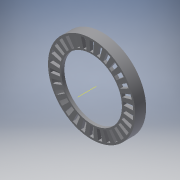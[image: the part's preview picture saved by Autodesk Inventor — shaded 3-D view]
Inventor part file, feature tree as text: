
AUTODESK INVENTOR PART (.ipt)
format: ipt  version: 2016 (Build 200138000, 138)  size: 313,344 bytes
history: native  units: mm
features: extrude x3, sketch x3, other x1, pattern_circular x1
ambient origin geometry x8: Origin, YZ Plane, XZ Plane, XY Plane, X Axis, Y Axis, Z Axis, Center Point
bodies: Body1 (feature_tree)
feature tree (8):
  extrude  "Extrusion3"  Depth=53.5mm
  extrude  "Extrusion4"  Depth=39.0mm
  other  "Work Axis3"
  pattern_circular  "Circular Pattern2"  [2 undecoded]
  extrude  "Extrusion5"  Depth=5.0mm
  sketch  "Sketch1"  dims[d0=56.0mm d1=53.5mm]
  sketch  "Sketch4"  dims[d2=41.0mm d3=39.0mm]
  sketch  "Sketch5"  dims[d13=8.5mm d17=3.0mm d18=3.0mm d19=4.0mm d20=4.0mm d21=2.0mm d22=0.0mm d23=56.0mm d24=53.5mm d25=41.0mm d26=39.0mm d27=8.5mm d28=1.0mm d29=1.0mm d30=1.304878mm d31=1.304878mm d32=10.0mm d33=0.0mm d34=300.0mm d35=360.0deg d37=5.0mm d38=0.0mm]
note: 2 required parameter values undecoded (feature->parameter linkage not recoverable at this tier; creation-order binding heuristic only, values carry confidence <= 0.55)
